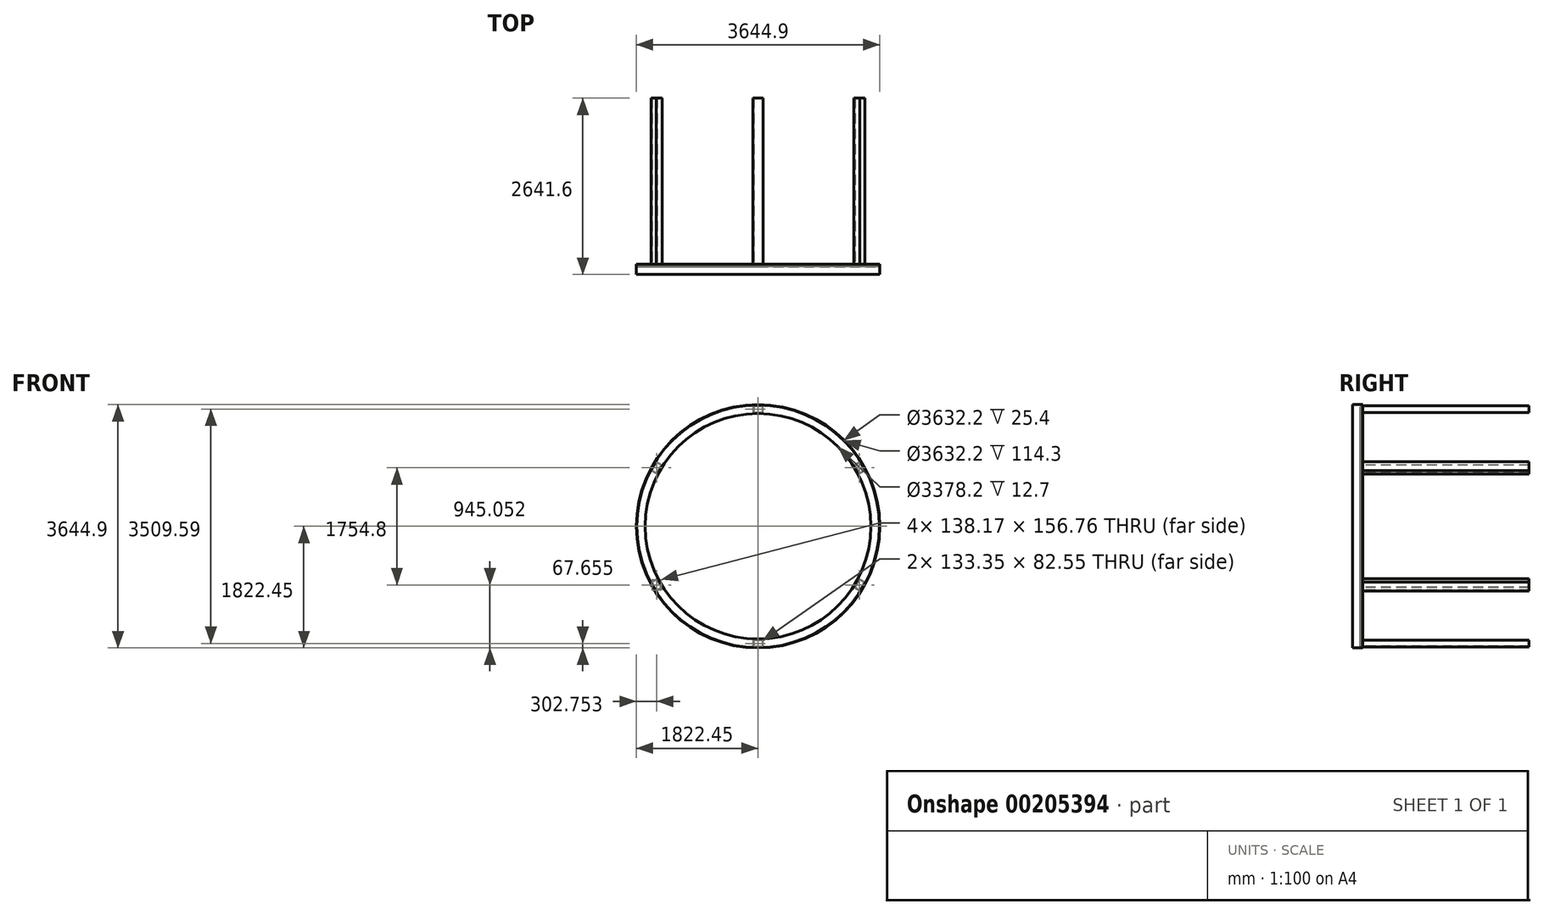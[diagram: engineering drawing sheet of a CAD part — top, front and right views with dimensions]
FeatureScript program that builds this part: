
annotation { "Feature Type Name" : "Feature", "Feature Type Description" : "" }
export const myFeature = defineFeature(function(context is Context, id is Id, definition is map)
    precondition{}
    {
        {
            var Q0;
            Q0=qCreatedBy(makeId("Front.planeOp"),FACE);
            var sketch = newSketch(context, id + "F0", { "sketchPlane" : qUnion([Q0])});
            skCircle(sketch, "E0", {"center": v(0, 0) * mm, "radius": 1816.1 * mm});
            skCircle(sketch, "E1.0", {"center": v(0, 0) * mm, "radius": 1822.45 * mm});
            skSolve(sketch);
        }
        {
            var Q0;
            Q0=makeQuery(id+"F0.imprint","IMPRINT",FACE,{"disambiguationData":[TD([[makeQuery(id+"F0.imprint","IMPRINT",EDGE,{"derivedFrom":sQuery(id+"F0.wireOp",EDGE,"E0")}),-1.0]])]});
            extrude(context, id + "F1", {"entities" : qUnion([Q0]), "depth" : 152.4 * mm});
        }
        {
            var Q0;
            Q0=qCreatedBy(makeId("Front.planeOp"),FACE);
            cPlane(context, id + "F2", {"entities" : qUnion([Q0]), "cplaneType" : CPlaneType.OFFSET, "offset" : 25.4 * mm, "width" : 152.4 * mm, "height" : 152.4 * mm});
        }
        {
            var Q0;
            Q0=qCreatedBy(id+"F2.planeOp",FACE);
            var sketch = newSketch(context, id + "F3", { "sketchPlane" : qUnion([Q0])});
            skCircle(sketch, "E2", {"center": v(0, 0) * mm, "radius": 1816.1 * mm});
            skCircle(sketch, "E3", {"center": v(0, 0) * mm, "radius": 1689.1 * mm});
            skSolve(sketch);
        }
        {
            var Q0;
            Q0 = qSketchRegion(id + "F3", true);
            extrude(context, id + "F4", {"entities" : qUnion([Q0]), "operationType" : NewBodyOperationType.ADD, "depth" : 12.7 * mm});
        }
        {
            var Q0;
            Q0=makeQuery(id+"F4.opExtrude","CAP_FACE",FACE,{"disambiguationData":[OSD([sQuery(id+"F3.wireOp",EDGE,"E2"),sQuery(id+"F3.wireOp",EDGE,"E3")])],"isStart":true});
            var sketch = newSketch(context, id + "F5", { "sketchPlane" : qUnion([Q0])});
            skLineSegment(sketch, "E4", {"start": v(0, -1805.6) * mm, "end": v(-76.2, -1805.6) * mm});
            skLineSegment(sketch, "E5", {"start": v(-76.2, -1805.6) * mm, "end": v(-76.2, -1704) * mm});
            skLineSegment(sketch, "E6", {"start": v(-76.2, -1704) * mm, "end": v(76.2, -1704) * mm});
            skLineSegment(sketch, "E7", {"start": v(76.2, -1704) * mm, "end": v(76.2, -1805.6) * mm});
            skLineSegment(sketch, "E8", {"start": v(76.2, -1805.6) * mm, "end": v(0, -1805.6) * mm});
            skLineSegment(sketch, "E9.0", {"start": v(66.67, -1713.52) * mm, "end": v(66.67, -1796.07) * mm});
            skLineSegment(sketch, "E9.1", {"start": v(-66.68, -1713.52) * mm, "end": v(66.67, -1713.52) * mm});
            skLineSegment(sketch, "E9.2", {"start": v(66.67, -1796.07) * mm, "end": v(0, -1796.07) * mm});
            skLineSegment(sketch, "E9.3", {"start": v(0, -1796.07) * mm, "end": v(-66.68, -1796.07) * mm});
            skLineSegment(sketch, "E9.4", {"start": v(-66.68, -1796.07) * mm, "end": v(-66.68, -1713.52) * mm});
            skSolve(sketch);
        }
        {
            var Q0;
            Q0=makeQuery(id+"F5.imprint","IMPRINT",FACE,{"disambiguationData":[TD([[makeQuery(id+"F5.imprint","IMPRINT",EDGE,{"derivedFrom":sQuery(id+"F5.wireOp",EDGE,"E4")}),-1.0]])]});
            extrude(context, id + "F6", {"entities" : qUnion([Q0]), "depth" : 2514.6 * mm});
        }
        {
            var Q0;
            Q0=makeQuery(id+"F6.opExtrude","SWEPT_BODY",BODY,{"disambiguationData":[OSD([sQuery(id+"F5.wireOp",EDGE,"E4"),sQuery(id+"F5.wireOp",EDGE,"E5"),sQuery(id+"F5.wireOp",EDGE,"E6"),sQuery(id+"F5.wireOp",EDGE,"E7"),sQuery(id+"F5.wireOp",EDGE,"E8"),sQuery(id+"F5.wireOp",EDGE,"E9.0"),sQuery(id+"F5.wireOp",EDGE,"E9.1"),sQuery(id+"F5.wireOp",EDGE,"E9.2"),sQuery(id+"F5.wireOp",EDGE,"E9.3"),sQuery(id+"F5.wireOp",EDGE,"E9.4")])]});
            var Q1;
            Q1=makeQuery(id+"F4.opExtrude","CAP_EDGE",EDGE,{"disambiguationData":[OSD([sQuery(id+"F3.wireOp",EDGE,"E3")])],"isStart":true});
            circularPattern(context, id + "F7", {"entities" : qUnion([Q0]), "axis" : qUnion([Q1]), "angle" : 360 * degree, "instanceCount" : 6, "equalSpace" : true, "computeTransformsWithoutBuiltin" : true});
        }
    });
